# Revit family: HERZ Commissioning Valve With Metering Station For Drinking Water Systems 4017 MW
name_source: partatom
category: Rohrzubehör
units: mm (PartAtom-declared; Revit-internal decimal feet)

## family parameters
Arbeitsebenenbasiert = Nein
Beim Laden mit Abzugskörper schneiden = Nein
Bemaßung runder Anschluss = Durchmesser verwenden
Gemeinsam genutzt = Nein
Immer vertikal = Ja
OmniClass-Nummer = 23.65.55.14
OmniClass-Titel = Valves for Liquid Services
Teiletyp = Unterbricht

## types (1)
- HERZ Commissioning Valve With Metering Station For Drinking Water Systems 4017 MW
    Application = For shutting off and regulating drinking water systems in buildings or for hydraulic balancing of supply lines.
    Body = DZR brass
    E00 = 0 mm  [stored 0 ft]
    H02 = 13 mm
    Hand wheel = plastic, green
    Hersteller = HERZ Armaturen Ges.m.b.H.
    Max. differential pressure on closed seat = 1000000.0 Pa
    Max. operating pressure at 20°C = 2000000.0 Pa
    Max. operating temperature at 10 bar = 85 °C
    Medium = Water
    Model = According to standard BS 7350 PN20 Series B
Angle seat regulating valve made of copper alloy.
All metal parts in contact with water are made of dezincification-resistant copper alloy.
The upper parts are equipped with non-rising stem.
    Note = Pursuant to Article 33 of the REACH Regulation (EC No. 1907/2006), we are obliged to point out that the material lead is listed on the SVHC list and that all brass components manufactured in our products exceed 0.1% (w / w) lead (CAS: 7439-92-1 / EINECS: 231-100-4).
Since lead is a component part of an alloy, actual exposure is not possible and therefore no additional information on safe use is necessary.
    O-Rings = EPDM
    R01 = 12 mm  [stored 0.0393701 ft]
    R02 = 9.5 mm  [stored 0.031168 ft]
    R03 = 21.5 mm  [stored 0.0705381 ft]
    S03 = 60 mm  [stored 0.19685 ft]
    SCRNCODE = 04;00;02
    SCRNSEQ = FW;SBT_TYP_FW="109";2
    SW01 = 60.00°
    URL = www.herzvalves.com
    Vorgabe-Ansicht = 0 mm  [stored 0 ft]
    W01 = 45.00°

note: [stored X ft] marks values corroborated as IEEE doubles in the binary element streams (Revit-internal decimal feet)
